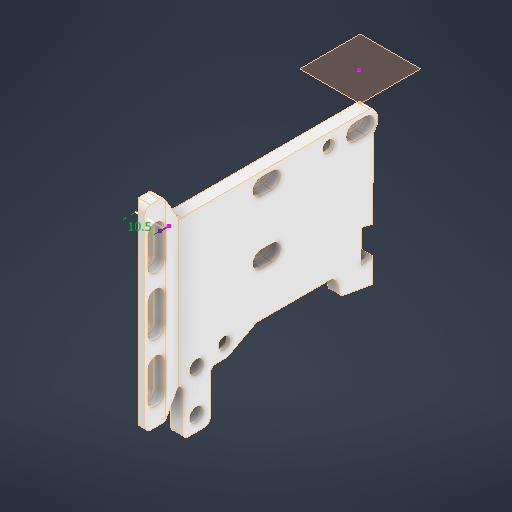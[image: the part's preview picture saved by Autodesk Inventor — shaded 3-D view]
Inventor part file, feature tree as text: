
AUTODESK INVENTOR PART (.ipt)
format: ipt  version: 2025 (Build 290162000, 162)  size: 612,352 bytes
history: native  units: mm
features: other x11, extrude x10, sketch x10, chamfer x3, reference x3, fillet x2, projected_geometry x2, plane x1
ambient origin geometry x8: Origin, YZ Plane, XZ Plane, XY Plane, X Axis, Y Axis, Z Axis, Center Point
bodies: Solid1 (feature_tree)
feature tree (42):
  extrude  "Extrusion3"  Depth=4.4mm TaperAngle=0.0deg
  extrude  "Extrusion4"  Depth=10.0mm
  plane  "Work Plane1"
  sketch  "Sketch13"  dims[d52=8.0mm d53=10.0mm d54=0.0mm]
  extrude  "Extrusion12"  Depth=10.0mm TaperAngle=0.0deg
  extrude  "Extrusion13"  Depth=4.75mm TaperAngle=0.0deg
  extrude  "Extrusion14"  Depth=10.0mm TaperAngle=45.0deg
  chamfer  "Chamfer3"  Distance=4.75mm
  chamfer  "Chamfer4"  Distance=3.0mm
  extrude  "Extrusion15"  Depth=2.0mm TaperAngle=45.0deg
  extrude  "Extrusion16"  Depth=5.0mm
  extrude  "Extrusion17"  Depth=18.0mm
  chamfer  "Chamfer5"  Distance=12.5mm
  fillet  "Fillet5"  Radius=5.0mm
  sketch  "Sketch20"  dims[d91=5.0mm d92=12.5mm d93=5.0mm d94=10.0mm d95=0.0mm d96=10.0mm d97=0.0mm d98=2.0mm d99=3.0mm d100=3.0mm d101=5.0mm d102=3.2mm d103=5.0mm d104=3.2mm d105=5.0mm d106=3.2mm d107=6.0mm d108=6.0mm d109=6.0mm]
  extrude  "Extrusion18"  Depth=10.0mm TaperAngle=0.0deg
  extrude  "Extrusion19"  Depth=10.0mm TaperAngle=0.0deg
  fillet  "Fillet6"  Radius=2.0mm
  sketch  "Sketch4"  dims[d15=4.4mm d16=0.0mm d19=4.5mm d20=0.0mm]
  sketch  "Sketch5"  dims[d50=10.5mm d51=10.0mm]
  reference  "Reference9"
  sketch  "Sketch14"  dims[d55=14.0mm d56=0.0mm d57=4.75mm d58=0.0mm]
  sketch  "Sketch15"  dims[d59=10.0mm d60=14.0mm d61=45.0deg d62=10.0mm d63=4.75mm d64=45.0deg d65=4.75mm d66=0.0mm d70=3.0mm d71=0.0mm]
  sketch  "Sketch16"  dims[d81=7.0mm d82=0.0mm d83=2.0mm d84=2.0mm d85=45.0deg]
  sketch  "Sketch17"  dims[d86=2.0mm d87=5.0mm]
  sketch  "Sketch18"  dims[d88=10.0mm d89=18.0mm]
  reference  "Reference31"
  reference  "Reference32"
  sketch  "Sketch19"  dims[d90=5.5mm]
  projected_geometry  "Projected Loop2"
  projected_geometry  "Projected Loop3"
  other  "Part 2"
  other  "<userpath> 7 was better\Documents\GitHub\ReplicatorPlusConversion\CAD\hotend.iam"
  other  "hotend.iam"
  other  "rails-bolts:1"
  other  "Finish1"
  other  "Finish2"
  other  "Finish3"
  other  "Finish4"
  other  "Finish6"
  other  "Finish7"
  other  "Finish8"
